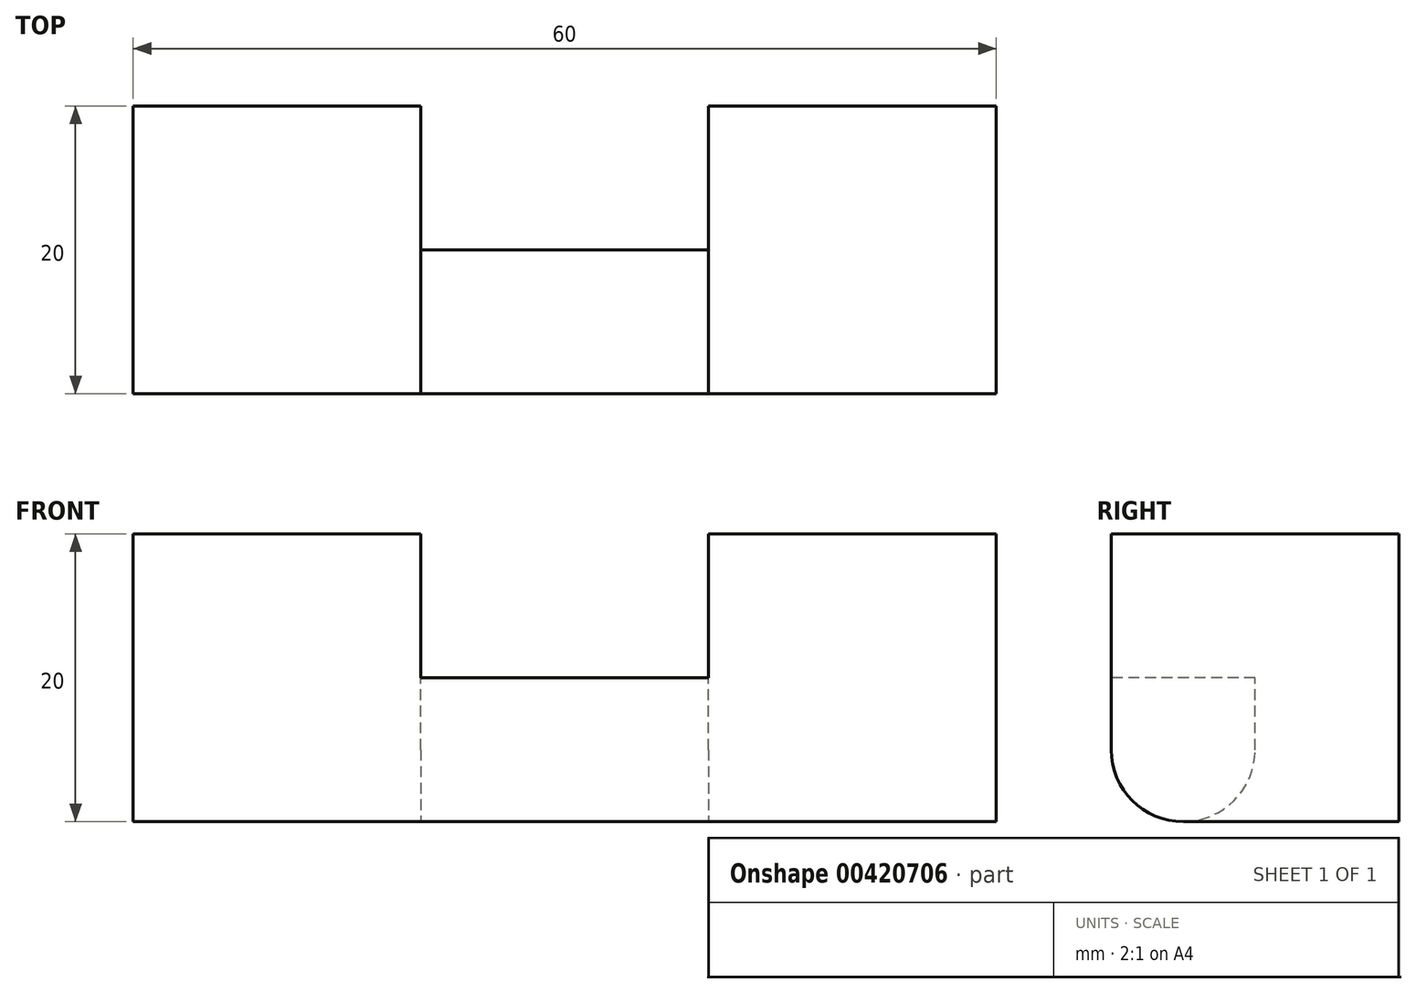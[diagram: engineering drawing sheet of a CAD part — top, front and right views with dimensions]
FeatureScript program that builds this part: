
annotation { "Feature Type Name" : "Feature", "Feature Type Description" : "" }
export const myFeature = defineFeature(function(context is Context, id is Id, definition is map)
    precondition{}
    {
        {
            var Q0;
            Q0=qCreatedBy(makeId("Right.planeOp"),FACE);
            var sketch = newSketch(context, id + "F0", { "sketchPlane" : qUnion([Q0])});
            skLineSegment(sketch, "E0.bottom", {"start": v(10, 10) * mm, "end": v(-10, 10) * mm});
            skLineSegment(sketch, "E0.top", {"start": v(10, -10) * mm, "end": v(-10, -10) * mm});
            skLineSegment(sketch, "E0.left", {"start": v(10, 10) * mm, "end": v(10, -10) * mm});
            skLineSegment(sketch, "E0.right", {"start": v(-10, 10) * mm, "end": v(-10, -10) * mm});
            skPoint(sketch, "E0.middle", {"position": v(0, 0) * mm});
            skSolve(sketch);
        }
        {
            var Q0;
            Q0=qSketchRegion(id+"F0",true);
            extrude(context, id + "F1", {"entities" : qUnion([Q0]), "endBound" : BoundingType.SYMMETRIC, "depth" : 60 * mm});
        }
        {
            var Q0;
            Q0=makeQuery(id+"F1.opExtrude","SWEPT_FACE",FACE,{"disambiguationData":[OSD([sQuery(id+"F0.wireOp",EDGE,"E0.right")])]});
            var sketch = newSketch(context, id + "F2", { "sketchPlane" : qUnion([Q0])});
            skLineSegment(sketch, "E1.bottom", {"start": v(-10, 10) * mm, "end": v(10, 10) * mm});
            skLineSegment(sketch, "E1.top", {"start": v(-10, 0) * mm, "end": v(10, 0) * mm});
            skLineSegment(sketch, "E1.left", {"start": v(-10, 10) * mm, "end": v(-10, 0) * mm});
            skLineSegment(sketch, "E1.right", {"start": v(10, 10) * mm, "end": v(10, 0) * mm});
            skSolve(sketch);
        }
        {
            var Q0;
            Q0=qSketchRegion(id+"F2",true);
            extrude(context, id + "F3", {"entities" : qUnion([Q0]), "operationType" : NewBodyOperationType.REMOVE, "oppositeDirection" : true, "depth" : 20 * mm});
        }
        {
            var Q0;
            Q0=makeQuery(id+"F3.boolean.opBoolean","COPY",FACE,{"derivedFrom":makeQuery(id+"F3.opExtrude","SWEPT_FACE",FACE,{"disambiguationData":[OSD([sQuery(id+"F2.wireOp",EDGE,"E1.top")])]})});
            var sketch = newSketch(context, id + "F4", { "sketchPlane" : qUnion([Q0])});
            skLineSegment(sketch, "E2.bottom", {"start": v(-10, 10) * mm, "end": v(10, 10) * mm});
            skLineSegment(sketch, "E2.top", {"start": v(-10, 0) * mm, "end": v(10, 0) * mm});
            skLineSegment(sketch, "E2.left", {"start": v(-10, 10) * mm, "end": v(-10, 0) * mm});
            skLineSegment(sketch, "E2.right", {"start": v(10, 10) * mm, "end": v(10, 0) * mm});
            skSolve(sketch);
        }
        {
            var Q0;
            Q0 = qSketchRegion(id + "F4", true);
            extrude(context, id + "F5", {"entities" : qUnion([Q0]), "operationType" : NewBodyOperationType.REMOVE, "oppositeDirection" : true, "depth" : 25 * mm});
        }
        {
            var Q0;
            Q0=makeQuery(id+"F5.boolean.opBoolean","COPY",EDGE,{"derivedFrom":makeQuery(id+"F5.opExtrude","CAP_EDGE",EDGE,{"disambiguationData":[OSD([sQuery(id+"F4.wireOp",EDGE,"E2.top")])],"isStart":true})});
            var Q1;
            Q1=makeQuery(id+"F5.boolean.opBoolean","INTERSECT",EDGE,{"derivedFrom":[makeQuery(id+"F1.opExtrude","SWEPT_FACE",FACE,{"disambiguationData":[OSD([sQuery(id+"F0.wireOp",EDGE,"E0.top")])]}),makeQuery(id+"F5.opExtrude","SWEPT_FACE",FACE,{"disambiguationData":[OSD([sQuery(id+"F4.wireOp",EDGE,"E2.top")])]})]});
            var Q2;
            Q2=makeQuery(id+"F3.boolean.opBoolean","COPY",EDGE,{"derivedFrom":makeQuery(id+"F3.opExtrude","CAP_EDGE",EDGE,{"disambiguationData":[OSD([sQuery(id+"F2.wireOp",EDGE,"E1.top")])],"isStart":true})});
            var Q3;
            Q3=makeQuery(id+"F1.opExtrude","SWEPT_EDGE",EDGE,{"disambiguationData":[OSD([sQuery(id+"F0.wireOp",EDGE,"E0.top"),sQuery(id+"F0.wireOp",EDGE,"E0.right")])]});
            fillet(context, id + "F6", {"entities" : qUnion([Q0, Q1, Q2, Q3]), "radius" : 5 * mm, "tangentPropagation" : true, "allowEdgeOverflow" : false});
        }
    });
